# Revit family: Chemseal
name_source: partatom
category: Specialty Equipment
units: mm (PartAtom-declared; Revit-internal decimal feet)

## family parameters
Cut with Voids When Loaded = No
Host = Face
Part Type = Normal
Room Calculation Point = No
Round Connector Dimension = Use Diameter
Shared = No

## types (1)
- SEE TYPE CATEGORY
    ABAA Compliance = Yes
    Assembly Code = C3020200
    Default Elevation = 0"
    Depth = 4"
    Description = Chemical-Resistant, Structural Expansion Joint and Construction Joint Sealant
    Durometer Hardness of Silicone Coating (ASTM D2240) = Shore A: 35
    Manufacturer = EMSEAL Joint Systems Ltd
    Model = Chemseal
    Movement (of Nominal Material Size) = +25% / -25%
    Pick Resistance = No
    Product Data URL = https://bit.ly
    Product Documentation URL = https://bit.ly
    Product Page URL = https://bit.ly
    Quad Deep Bellow = No
    Quad Shallow Bellow = No
    R Value Range (ASTM C518) = 2.1 per 1-inch (25mm) depth
    Rate of Air Leakage (ASTM E283) = Passed
    Seal Material Note = Chemseal is also available with a polysulfide coating
    Single Deep Bellow = No
    Single Shallow Bellow = Yes
    Staining (ASTM C510) = None
    Temperature Range (ASTM C711) = 185°F (85°C) to -40°F (-40°C)
    Tensile Strength (ASTM D3574) = 275 psi min
    Triple Bellow = No
    Triple Deep Bellow = No
    Triple Shallow Bellow = No
    Type Image = EMSEAL Chemseal.jpg
    URL = http://www.emseal.com
    Width = 1/2"

## geometry (parser evidence)
native form markers: Sweep x2
no freeform markers — native parametric forms only
